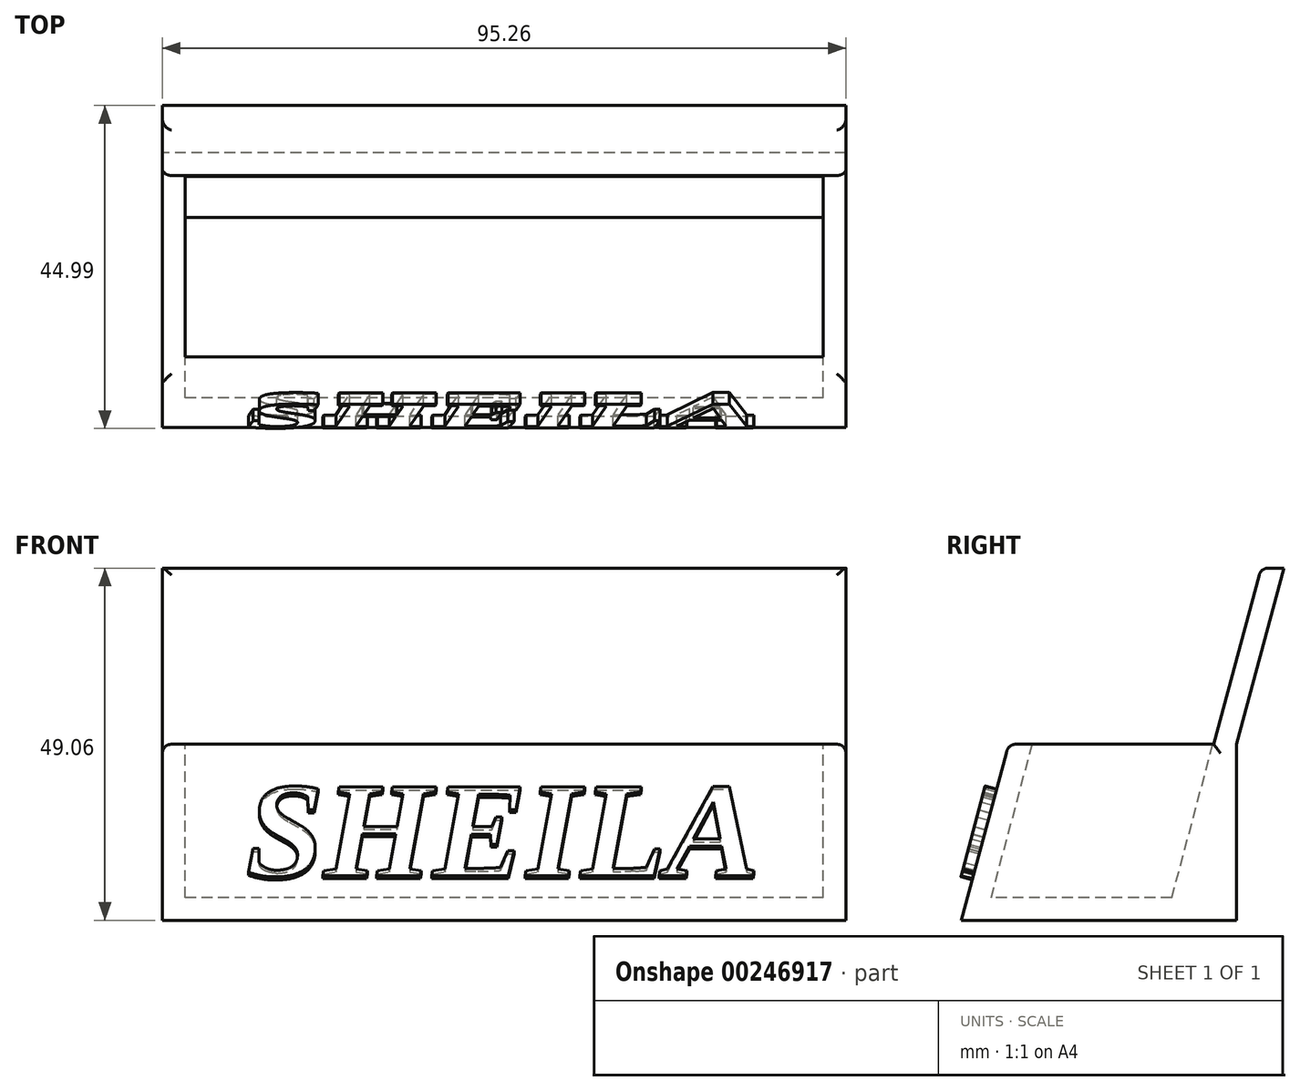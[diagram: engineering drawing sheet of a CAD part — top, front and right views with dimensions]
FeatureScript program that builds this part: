
annotation { "Feature Type Name" : "Feature", "Feature Type Description" : "" }
export const myFeature = defineFeature(function(context is Context, id is Id, definition is map)
    precondition{}
    {
        {
            var Q0;
            Q0=qCreatedBy(makeId("Right.planeOp"),FACE);
            var sketch = newSketch(context, id + "F0", { "sketchPlane" : qUnion([Q0])});
            skLineSegment(sketch, "E0.bottom", {"start": v(9.3, -24.53) * mm, "end": v(-22.45, -24.53) * mm});
            skLineSegment(sketch, "E0.top", {"start": v(22.45, 24.53) * mm, "end": v(-9.3, 24.53) * mm});
            skLineSegment(sketch, "E0.left", {"start": v(9.3, -24.53) * mm, "end": v(22.45, 24.53) * mm});
            skLineSegment(sketch, "E0.right", {"start": v(-22.45, -24.53) * mm, "end": v(-9.3, 24.53) * mm});
            skPoint(sketch, "E0.middle", {"position": v(0, 0) * mm});
            skLineSegment(sketch, "E1", {"start": v(-15.88, 0) * mm, "end": v(12.7, 0) * mm});
            skLineSegment(sketch, "E2", {"start": v(12.7, 0) * mm, "end": v(19.27, 24.53) * mm});
            skLineSegment(sketch, "E3", {"start": v(15.88, 0) * mm, "end": v(15.88, -24.53) * mm});
            skLineSegment(sketch, "E4", {"start": v(9.3, -24.53) * mm, "end": v(15.88, -24.53) * mm});
            skSolve(sketch);
        }
        {
            var Q0;
            {var subQ1=sQuery(id+"F0.wireOp",EDGE,"E0.bottom");Q0=makeQuery(id+"F0.imprint","IMPRINT",FACE,{"disambiguationData":[TD([[makeQuery(id+"F0.imprint","IMPRINT",EDGE,{"derivedFrom":subQ1}),-1.0]])]});}
            extrude(context, id + "F1", {"entities" : qUnion([Q0]), "endBound" : BoundingType.SYMMETRIC, "depth" : 95.25 * mm});
        }
        {
            var Q0;
            Q0=makeQuery(id+"F1.opExtrude","SWEPT_FACE",FACE,{"disambiguationData":[OSD([sQuery(id+"F0.wireOp",EDGE,"E1")])]});
            shell(context, id + "F2", {"entities" : qUnion([Q0]), "thickness" : 3.17 * mm});
        }
        {
            var Q0;
            {var subQ2=sQuery(id+"F0.wireOp",EDGE,"E3");Q0=makeQuery(id+"F0.imprint","IMPRINT",FACE,{"disambiguationData":[TD([[makeQuery(id+"F0.imprint","IMPRINT",EDGE,{"derivedFrom":subQ2}),-1.0]])]});}
            extrude(context, id + "F3", {"entities" : qUnion([Q0]), "operationType" : NewBodyOperationType.ADD, "endBound" : BoundingType.SYMMETRIC, "depth" : 95.25 * mm});
        }
        {
            var Q0;
            Q0=makeQuery(id+"F1.opExtrude","SWEPT_EDGE",EDGE,{"disambiguationData":[OSD([sQuery(id+"F0.wireOp",EDGE,"E0.top"),sQuery(id+"F0.wireOp",EDGE,"E2")])]});
            var Q1;
            Q1=makeQuery(id+"F1.opExtrude","CAP_EDGE",EDGE,{"disambiguationData":[OSD([sQuery(id+"F0.wireOp",EDGE,"E2")])],"isStart":true});
            var Q2;
            Q2=makeQuery(id+"F1.opExtrude","CAP_EDGE",EDGE,{"disambiguationData":[OSD([sQuery(id+"F0.wireOp",EDGE,"E2")])],"isStart":false});
            var Q3;
            Q3=makeQuery(id+"F1.opExtrude","CAP_EDGE",EDGE,{"disambiguationData":[OSD([sQuery(id+"F0.wireOp",EDGE,"E1")])],"isStart":true});
            var Q4;
            Q4=makeQuery(id+"F1.opExtrude","SWEPT_EDGE",EDGE,{"disambiguationData":[OSD([sQuery(id+"F0.wireOp",EDGE,"E0.right"),sQuery(id+"F0.wireOp",EDGE,"E1")])]});
            var Q5;
            Q5=makeQuery(id+"F1.opExtrude","CAP_EDGE",EDGE,{"disambiguationData":[OSD([sQuery(id+"F0.wireOp",EDGE,"E1")])],"isStart":false});
            fillet(context, id + "F4", {"entities" : qUnion([Q0, Q1, Q2, Q3, Q4, Q5]), "radius" : 1.27 * mm, "tangentPropagation" : true, "allowEdgeOverflow" : false});
        }
        {
            var Q0;
            Q0=makeQuery(id+"F1.opExtrude","SWEPT_FACE",FACE,{"disambiguationData":[OSD([sQuery(id+"F0.wireOp",EDGE,"E0.right")])]});
            var sketch = newSketch(context, id + "F5", { "sketchPlane" : qUnion([Q0])});
            skText(sketch, "E5", { "text": "SHEILA", "fontName": "Tinos-BoldItalic.ttf"});
            const initialGuessF5  = {"E5": [-0.03596, -0.0235, 1, 0, 0.01405]};
            skSetInitialGuess(sketch, initialGuessF5);
            skSolve(sketch);
        }
        {
            var Q0;
            Q0 = qSketchRegion(id + "F5", true);
            extrude(context, id + "F6", {"entities" : qUnion([Q0]), "operationType" : NewBodyOperationType.ADD, "depth" : 1.65 * mm});
        }
    });
